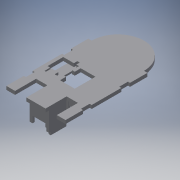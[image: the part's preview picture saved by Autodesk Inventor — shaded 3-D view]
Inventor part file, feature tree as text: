
AUTODESK INVENTOR PART (.ipt)
format: ipt  version: 2016 (Build 200138000, 138)  size: 534,016 bytes
history: native  units: in
note: dims shown in document units (in); Inventor stores cm internally (conversion verified against a paired STEP export)
features: reference x40, extrude x28, sketch x28, plane x6, projected_geometry x2
ambient origin geometry x8: Origin, YZ Plane, XZ Plane, XY Plane, X Axis, Y Axis, Z Axis, Center Point
bodies: Solid1 (feature_tree)
feature tree (104):
  extrude  "Extrusion1"  Depth=3.0in
  extrude  "Extrusion2"  Depth=0.0787in
  extrude  "Extrusion3"  Depth=1.0in
  extrude  "Extrusion5"  Depth=1.0in TaperAngle=0.0deg
  plane  "Work Plane1"
  extrude  "Extrusion6"  Depth=0.0787in
  extrude  "Extrusion9"  Depth=0.0787in
  extrude  "Extrusion14"  Depth=0.1575in
  extrude  "Extrusion15"  Depth=1.25in
  plane  "Work Plane2"
  extrude  "Extrusion16"  Depth=0.1575in
  extrude  "Extrusion17"  Depth=0.9201in TaperAngle=0.0deg
  extrude  "Extrusion18"  Depth=0.1969in
  plane  "Work Plane3"
  extrude  "Extrusion20"  Depth=0.1969in TaperAngle=0.0deg
  extrude  "Extrusion21"  Depth=0.1181in TaperAngle=0.0deg
  plane  "Work Plane4"
  plane  "Work Plane5"
  extrude  "Extrusion23"  Depth=0.1181in
  extrude  "Extrusion24"  Depth=0.1969in TaperAngle=0.0deg
  plane  "Work Plane6"
  extrude  "Extrusion25"  Depth=0.35in
  extrude  "Extrusion26"  Depth=0.2in
  extrude  "Extrusion27"  Depth=0.1969in TaperAngle=0.0deg
  extrude  "Extrusion28"  Depth=1.5in
  extrude  "Extrusion29"  Depth=0.7in
  extrude  "Extrusion30"  Depth=0.1181in TaperAngle=0.0deg
  extrude  "Extrusion31"  Depth=1.0in
  extrude  "Extrusion34"  Depth=0.5in
  sketch  "Sketch36"  dims[d105=0.1181in d106=0.5in]
  extrude  "Extrusion35"  Depth=0.5in
  extrude  "Extrusion36"  Depth=0.0197in
  extrude  "Extrusion37"  Depth=0.325in
  extrude  "Extrusion38"  Depth=0.1969in
  extrude  "Extrusion39"  Depth=0.1181in
  sketch  "Sketch41"  dims[d117=0.1969in d118=0.1181in d119=0.1969in d120=0.0in d121=0.1575in d122=0.0in d123=0.1in d124=0.0in d132=1.0in d133=0.0in d134=0.5in d135=0.5in d136=0.0039in d137=0.0039in d138=0.0984in d139=0.0984in d140=0.0039in d141=0.0984in d142=1.61in d143=0.0in d144=0.2in d145=0.0in d146=0.1181in d147=0.85in d148=0.0in d149=1.2in d150=0.1181in d151=1.1in d152=0.0in d153=0.28in d154=3.0in d155=0.0in]
  sketch  "Sketch1"  dims[d0=4.5in d1=3.0in]
  sketch  "Sketch2"  dims[d2=0.1969in d3=0.0in d5=0.0787in]
  reference  "Reference1"
  reference  "Reference2"
  sketch  "Sketch3"  dims[d6=1.0in d7=0.0in d8=1.0827in]
  sketch  "Sketch5"  dims[d9=0.3937in d10=1.0in d11=0.0in]
  reference  "Reference14"
  reference  "Reference15"
  reference  "Reference16"
  reference  "Reference17"
  reference  "Reference18"
  sketch  "Sketch6"  dims[d12=0.0787in d23=0.0098in]
  reference  "Reference19"
  sketch  "Sketch9"  dims[d24=0.1575in d25=0.0787in]
  projected_geometry  "Projected Loop2"
  sketch  "Sketch14"  dims[d26=0.0098in d27=0.1575in]
  sketch  "Sketch15"  dims[d28=0.1181in d29=0.0in d30=1.25in]
  sketch  "Sketch16"  dims[d31=0.1575in d32=0.1575in]
  reference  "Reference30"
  sketch  "Sketch17"  dims[d33=0.1181in d34=0.0in d46=0.9201in d47=0.0in]
  reference  "Reference31"
  reference  "Reference32"
  reference  "Reference33"
  reference  "Reference35"
  reference  "Reference36"
  reference  "Reference37"
  reference  "Reference38"
  reference  "Reference39"
  reference  "Reference40"
  reference  "Reference41"
  reference  "Reference42"
  reference  "Reference43"
  reference  "Reference44"
  reference  "Reference45"
  reference  "Reference46"
  reference  "Reference47"
  reference  "Reference48"
  reference  "Reference49"
  sketch  "Sketch20"  dims[d58=0.1969in d59=0.1969in]
  reference  "Reference50"
  sketch  "Sketch21"  dims[d60=0.1969in d61=0.1969in d62=0.0in]
  sketch  "Sketch23"  dims[d63=1.0in d64=0.0in d65=0.1181in d66=0.0in]
  reference  "Reference53"
  reference  "Reference54"
  sketch  "Sketch24"  dims[d67=0.1969in d68=0.0in d69=0.1181in]
  sketch  "Sketch25"  dims[d70=0.1181in d71=0.1969in d72=0.0in]
  reference  "Reference55"
  reference  "Reference56"
  sketch  "Sketch26"  dims[d75=0.0394in d76=0.35in]
  reference  "Reference57"
  reference  "Reference58"
  sketch  "Sketch28"  dims[d77=0.1628in d78=0.2in]
  sketch  "Sketch29"  dims[d79=0.0787in d80=0.0in d81=0.1969in d82=0.0in]
  sketch  "Sketch30"  dims[d89=1.5in d90=1.5in]
  reference  "Reference59"
  sketch  "Sketch31"  dims[d91=0.1181in d92=0.0in d93=0.7in]
  sketch  "Sketch32"  dims[d94=1.26in d95=0.0in d96=0.1181in d97=0.0in]
  sketch  "Sketch35"  dims[d98=0.1181in d99=0.0in d104=1.0in]
  reference  "Reference61"
  sketch  "Sketch37"  dims[d107=1.0in d108=0.5in]
  reference  "Reference62"
  sketch  "Sketch38"  dims[d109=10.0in d110=0.0in d111=0.0197in]
  reference  "Reference63"
  sketch  "Sketch39"  dims[d112=0.0197in d113=0.325in]
  reference  "Reference64"
  sketch  "Sketch40"  dims[d114=0.197in d115=0.0in d116=0.1969in]
  reference  "Reference65"
  projected_geometry  "Projected Loop6"
